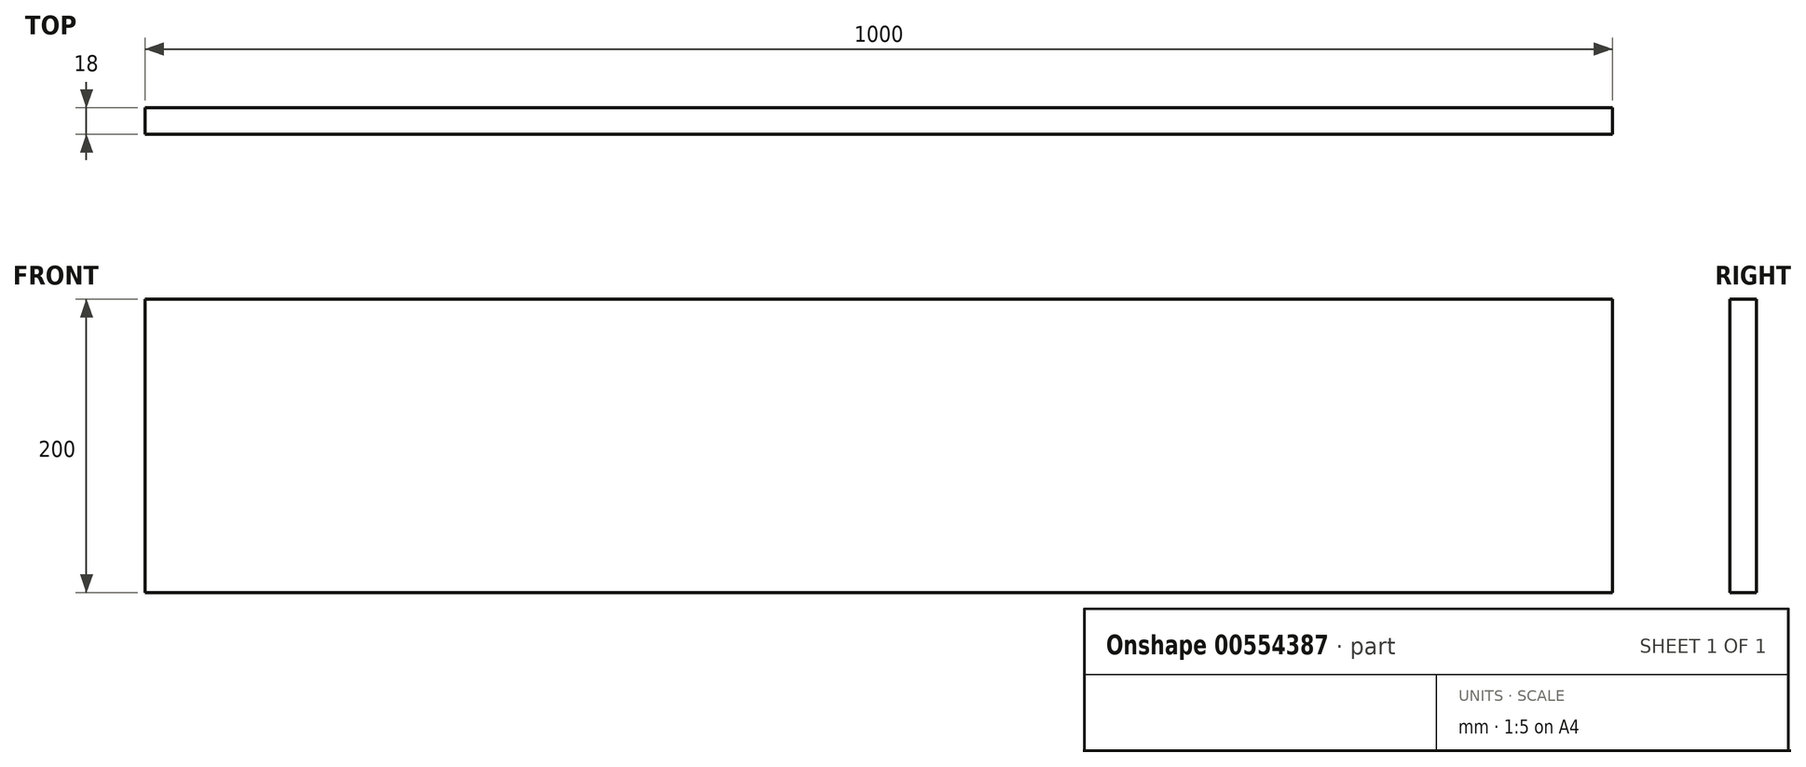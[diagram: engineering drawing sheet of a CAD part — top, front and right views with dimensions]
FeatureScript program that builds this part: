
annotation { "Feature Type Name" : "Feature", "Feature Type Description" : "" }
export const myFeature = defineFeature(function(context is Context, id is Id, definition is map)
    precondition{}
    {
        {
            var Q0;
            Q0=qCreatedBy(makeId("Front.planeOp"),FACE);
            var sketch = newSketch(context, id + "F0", { "sketchPlane" : qUnion([Q0])});
            skLineSegment(sketch, "E0.bottom", {"start": v(0, 0) * mm, "end": v(1000, 0) * mm});
            skLineSegment(sketch, "E0.top", {"start": v(0, 200) * mm, "end": v(1000, 200) * mm});
            skLineSegment(sketch, "E0.left", {"start": v(0, 0) * mm, "end": v(0, 200) * mm});
            skLineSegment(sketch, "E0.right", {"start": v(1000, 0) * mm, "end": v(1000, 200) * mm});
            skSolve(sketch);
        }
        {
            var Q0;
            Q0=makeQuery(id+"F0.imprint","IMPRINT",FACE,{"disambiguationData":[TD([[makeQuery(id+"F0.imprint","IMPRINT",EDGE,{"derivedFrom":sQuery(id+"F0.wireOp",EDGE,"E0.bottom")}),1.0]])]});
            extrude(context, id + "F1", {"entities" : qUnion([Q0]), "depth" : 18 * mm, "offsetDistance" : 25 * mm});
        }
    });
